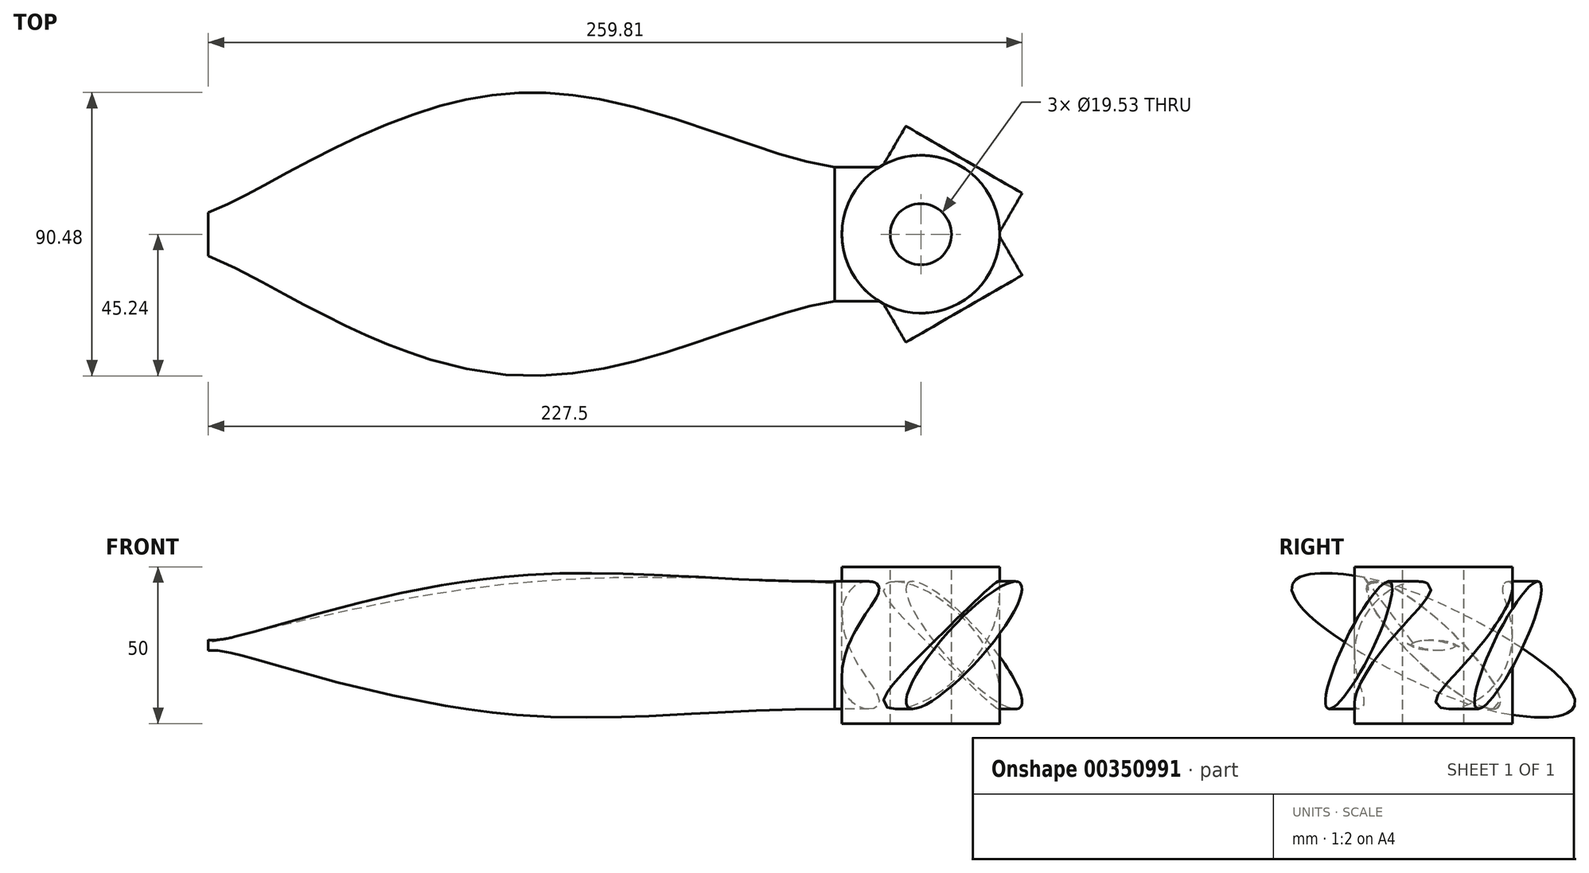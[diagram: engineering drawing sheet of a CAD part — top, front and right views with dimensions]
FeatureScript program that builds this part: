
annotation { "Feature Type Name" : "Feature", "Feature Type Description" : "" }
export const myFeature = defineFeature(function(context is Context, id is Id, definition is map)
    precondition{}
    {
        {
            var Q0;
            Q0=qCreatedBy(makeId("Right.planeOp"),FACE);
            var sketch = newSketch(context, id + "F0", { "sketchPlane" : qUnion([Q0])});
            skLineSegment(sketch, "E0.bottom", {"start": v(-213.06, 65.62) * mm, "end": v(-238.25, 65.62) * mm});
            skLineSegment(sketch, "E0.top", {"start": v(-213.06, 15.62) * mm, "end": v(-238.25, 15.62) * mm});
            skLineSegment(sketch, "E0.left", {"start": v(-213.06, 65.62) * mm, "end": v(-213.06, 15.62) * mm});
            skLineSegment(sketch, "E0.right", {"start": v(-238.25, 65.62) * mm, "end": v(-238.25, 15.62) * mm});
            skSolve(sketch);
        }
        {
            var Q0;
            Q0=qSketchRegion(id+"F0",true);
            var Q1;
            Q1=sQuery(id+"F0.wireOp",EDGE,"E0.left");
            revolve(context, id + "F1", {"entities" : qUnion([Q0]), "axis" : qUnion([Q1]), "revolveType" : RevolveType.FULL});
        }
        {
            var Q0;
            Q0=makeQuery(id+"F1.opRevolve","SWEPT_FACE",FACE,{"disambiguationData":[OSD([sQuery(id+"F0.wireOp",EDGE,"E0.bottom")])]});
            var sketch = newSketch(context, id + "F2", { "sketchPlane" : qUnion([Q0])});
            skCircle(sketch, "E1", {"center": v(0, -213.06) * mm, "radius": 9.76 * mm});
            skSolve(sketch);
        }
        {
            var Q0;
            Q0=makeQuery(id+"F0.imprint","IMPRINT",FACE,{"disambiguationData":[TD([[makeQuery(id+"F0.imprint","IMPRINT",EDGE,{"derivedFrom":sQuery(id+"F0.wireOp",EDGE,"E0.bottom")}),1.0]])]});
            var sketch = newSketch(context, id + "F3", { "sketchPlane" : qUnion([Q0])});
            skLineSegment(sketch, "E2.0", {"start": v(-213.06, 65.62) * mm, "end": v(-213.06, 15.62) * mm});
            skLineSegment(sketch, "E3.0", {"start": v(-238.25, 65.62) * mm, "end": v(-187.87, 65.62) * mm});
            skLineSegment(sketch, "E4.0", {"start": v(-238.25, 15.62) * mm, "end": v(-187.87, 15.62) * mm});
            skEllipse(sketch, "E5", {"center": v(-213.06, 40.62) * mm, "majorRadius": 28.71 * mm, "minorRadius": 7.07 * mm, "majorAxis": v(-0.73, 0.69)});
            skSolve(sketch);
        }
        {
            var Q0;
            Q0=qSketchRegion(id+"F3",true);
            extrude(context, id + "F4", {"entities" : qUnion([Q0]), "operationType" : NewBodyOperationType.ADD, "oppositeDirection" : true, "depth" : 27.5 * mm});
        }
        {
            var Q0;
            Q0=makeQuery(id+"F4.opExtrude","CAP_FACE",FACE,{"disambiguationData":[OSD([sQuery(id+"F3.wireOp",EDGE,"E5")])],"isStart":false});
            cPlane(context, id + "F5", {"entities" : qUnion([Q0]), "cplaneType" : CPlaneType.OFFSET, "offset" : 200 * mm, "width" : 150 * mm, "height" : 150 * mm});
        }
        {
            var Q0;
            Q0=qSketchRegion(id+"F2",true);
            var Q1;
            Q1=makeQuery(id+"F1.opRevolve","SWEPT_FACE",FACE,{"disambiguationData":[OSD([sQuery(id+"F0.wireOp",EDGE,"E0.top")])]});
            extrude(context, id + "F6", {"entities" : qUnion([Q0]), "operationType" : NewBodyOperationType.REMOVE, "endBound" : BoundingType.UP_TO_SURFACE, "oppositeDirection" : true, "endBoundEntityFace" : qUnion([Q1]), "depth" : 25 * mm});
        }
        {
            var Q0;
            Q0=makeQuery(id+"F1.opRevolve","SWEPT_BODY",BODY,{"disambiguationData":[OSD([sQuery(id+"F0.wireOp",EDGE,"E0.bottom"),sQuery(id+"F0.wireOp",EDGE,"E0.top"),sQuery(id+"F0.wireOp",EDGE,"E0.left"),sQuery(id+"F0.wireOp",EDGE,"E0.right")])]});
            var Q1;
            Q1=sQuery(id+"F0.wireOp",EDGE,"E0.left");
            circularPattern(context, id + "F7", {"entities" : qUnion([Q0]), "axis" : qUnion([Q1]), "angle" : 360 * degree, "instanceCount" : 3, "equalSpace" : true});
        }
        {
            var Q0;
            Q0=qCreatedBy(id+"F5.planeOp",FACE);
            cPlane(context, id + "F8", {"entities" : qUnion([Q0]), "cplaneType" : CPlaneType.OFFSET, "offset" : 100 * mm, "oppositeDirection" : true, "width" : 150 * mm, "height" : 150 * mm});
        }
        {
            var Q0;
            Q0=qCreatedBy(id+"F8.planeOp",FACE);
            var sketch = newSketch(context, id + "F9", { "sketchPlane" : qUnion([Q0])});
            skEllipse(sketch, "E6.0", {"center": v(213.06, 40.62) * mm, "majorRadius": 48.94 * mm, "minorRadius": 12.05 * mm, "majorAxis": v(0.92, 0.4)});
            skSolve(sketch);
        }
        {
            var Q0;
            Q0=qCreatedBy(id+"F5.planeOp",FACE);
            var sketch = newSketch(context, id + "F10", { "sketchPlane" : qUnion([Q0])});
            skEllipse(sketch, "E7.0", {"center": v(213.06, 40.62) * mm, "majorRadius": 6.95 * mm, "minorRadius": 1.71 * mm, "majorAxis": v(1, 0.02)});
            skSolve(sketch);
        }
        {
            var Q0;
            Q0=makeQuery(id+"F4.opExtrude","CAP_FACE",FACE,{"disambiguationData":[OSD([sQuery(id+"F3.wireOp",EDGE,"E5")])],"isStart":false});
            var Q1;
            Q1=makeQuery(id+"F9.imprint","IMPRINT",FACE,{"disambiguationData":[TD([[makeQuery(id+"F9.imprint","IMPRINT",EDGE,{"derivedFrom":sQuery(id+"F9.wireOp",EDGE,"E6.0")}),1.0]])]});
            var Q2;
            Q2=makeQuery(id+"F10.imprint","IMPRINT",FACE,{"disambiguationData":[TD([[makeQuery(id+"F10.imprint","IMPRINT",EDGE,{"derivedFrom":sQuery(id+"F10.wireOp",EDGE,"E7.0")}),1.0]])]});
            loft(context, id + "F11", {"sheetProfilesArray" : [{ "sheetProfileEntities" : qUnion([Q0]) }, { "sheetProfileEntities" : qUnion([Q1]) }, { "sheetProfileEntities" : qUnion([Q2]) }]});
        }
    });
